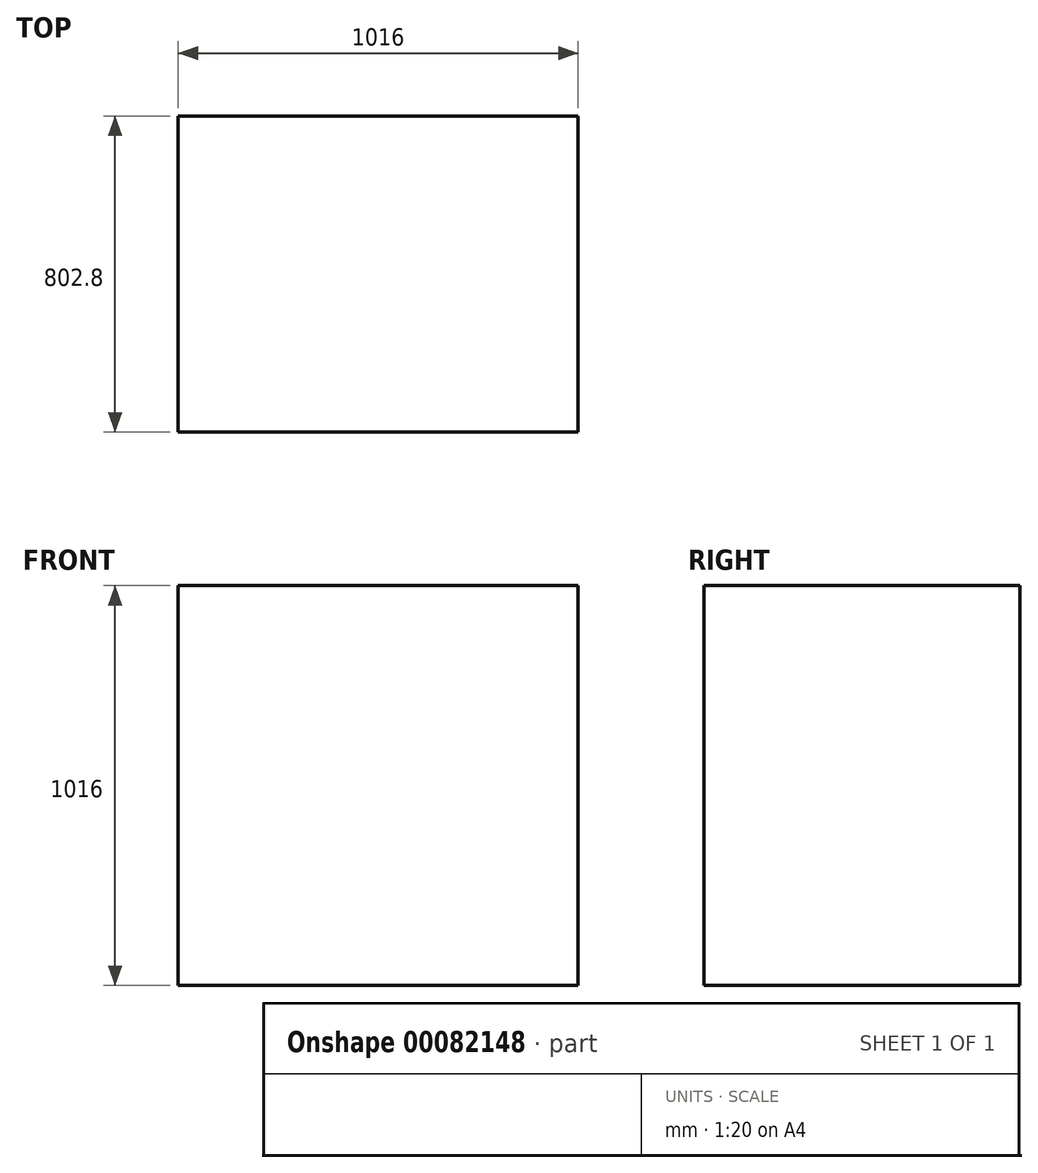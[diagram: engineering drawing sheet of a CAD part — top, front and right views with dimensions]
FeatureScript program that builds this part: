
annotation { "Feature Type Name" : "Feature", "Feature Type Description" : "" }
export const myFeature = defineFeature(function(context is Context, id is Id, definition is map)
    precondition{}
    {
        {
            var Q0;
            Q0=qCreatedBy(makeId("Top.planeOp"),FACE);
            var sketch = newSketch(context, id + "F0", { "sketchPlane" : qUnion([Q0])});
            skLineSegment(sketch, "E0.bottom", {"start": v(-508, 401.4) * mm, "end": v(508, 401.4) * mm});
            skLineSegment(sketch, "E0.top", {"start": v(-508, -401.4) * mm, "end": v(508, -401.4) * mm});
            skLineSegment(sketch, "E0.left", {"start": v(-508, 401.4) * mm, "end": v(-508, -401.4) * mm});
            skLineSegment(sketch, "E0.right", {"start": v(508, 401.4) * mm, "end": v(508, -401.4) * mm});
            skPoint(sketch, "E0.middle", {"position": v(0, 0) * mm});
            skSolve(sketch);
        }
        {
            var Q0;
            Q0 = qSketchRegion(id + "F0", true);
            extrude(context, id + "F1", {"entities" : qUnion([Q0]), "depth" : 1016 * mm});
        }
    });
